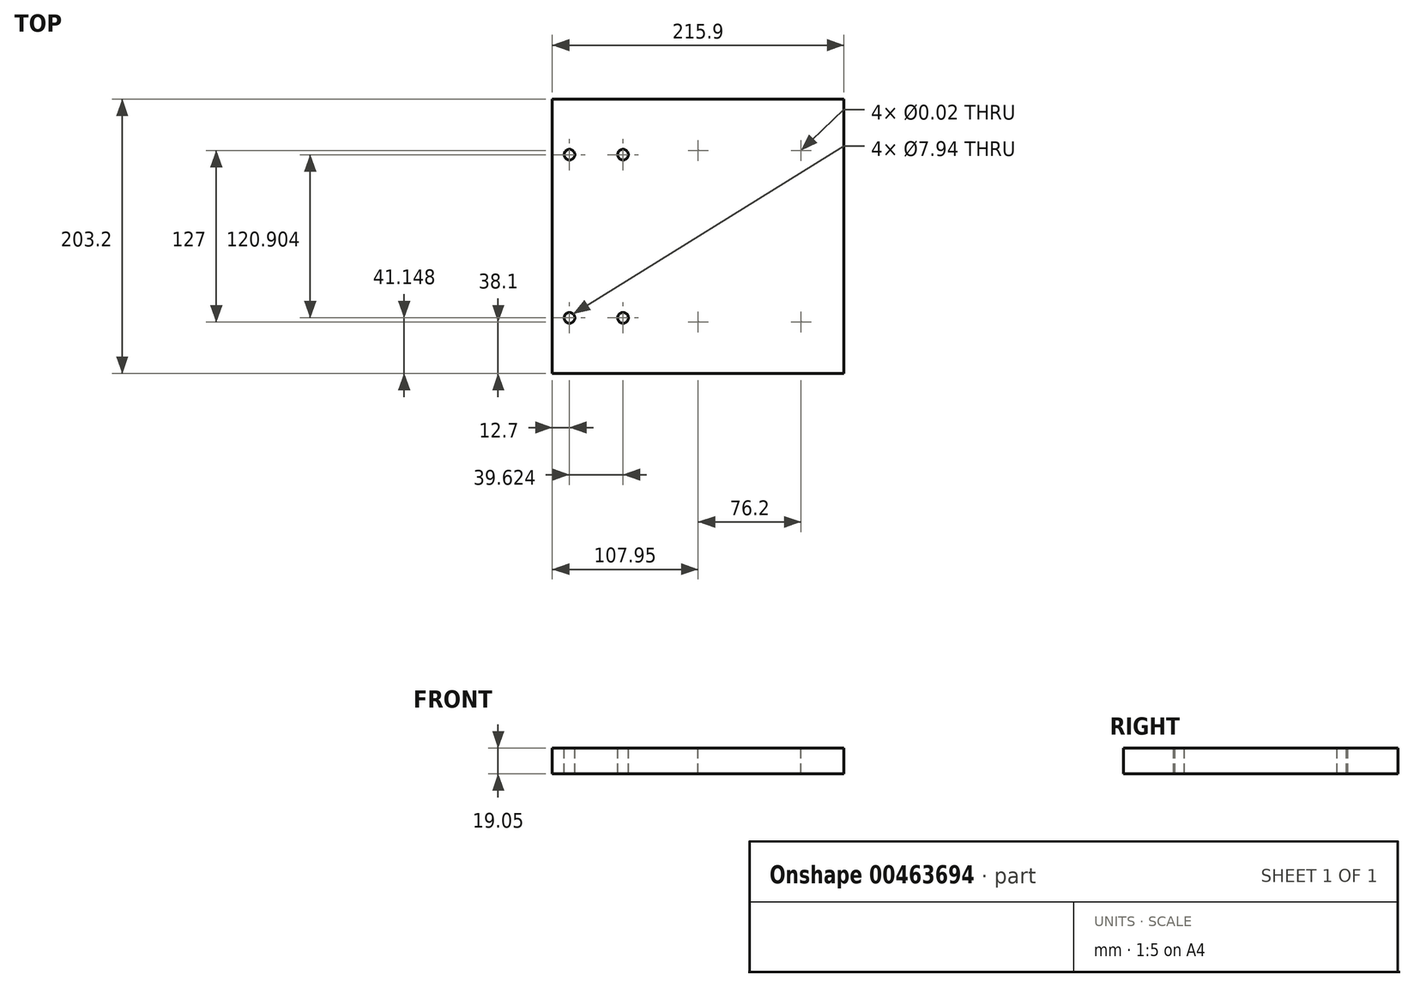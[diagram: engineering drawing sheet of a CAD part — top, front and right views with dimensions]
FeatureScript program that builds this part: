
annotation { "Feature Type Name" : "Feature", "Feature Type Description" : "" }
export const myFeature = defineFeature(function(context is Context, id is Id, definition is map)
    precondition{}
    {
        {
            var Q0;
            Q0=qCreatedBy(makeId("Top.planeOp"),FACE);
            var sketch = newSketch(context, id + "F0", { "sketchPlane" : qUnion([Q0])});
            skLineSegment(sketch, "E0.bottom", {"start": v(-107.95, 101.6) * mm, "end": v(107.95, 101.6) * mm});
            skLineSegment(sketch, "E0.top", {"start": v(-107.95, -101.6) * mm, "end": v(107.95, -101.6) * mm});
            skLineSegment(sketch, "E0.left", {"start": v(-107.95, 101.6) * mm, "end": v(-107.95, -101.6) * mm});
            skLineSegment(sketch, "E0.right", {"start": v(107.95, 101.6) * mm, "end": v(107.95, -101.6) * mm});
            skPoint(sketch, "E0.middle", {"position": v(0, 0) * mm});
            skSolve(sketch);
        }
        {
            var Q0;
            Q0 = qSketchRegion(id + "F0", true);
            extrude(context, id + "F1", {"entities" : qUnion([Q0]), "depth" : 19.05 * mm});
        }
        {
            var Q0;
            Q0=makeQuery(id+"F1.opExtrude","CAP_FACE",FACE,{"disambiguationData":[OSD([sQuery(id+"F0.wireOp",EDGE,"E0.bottom"),sQuery(id+"F0.wireOp",EDGE,"E0.top"),sQuery(id+"F0.wireOp",EDGE,"E0.left"),sQuery(id+"F0.wireOp",EDGE,"E0.right")])],"isStart":false});
            var sketch = newSketch(context, id + "F2", { "sketchPlane" : qUnion([Q0])});
            skLineSegment(sketch, "E1", {"start": v(-145.85, 0) * mm, "end": v(139, 0) * mm, "construction": true});
            skLineSegment(sketch, "E2.0", {"start": v(107.95, 101.6) * mm, "end": v(107.95, -101.6) * mm, "construction": true});
            skLineSegment(sketch, "E3.0", {"start": v(38.1, 101.6) * mm, "end": v(38.1, -101.6) * mm, "construction": true});
            skLineSegment(sketch, "E4.0", {"start": v(0, 101.6) * mm, "end": v(0, -101.6) * mm, "construction": true});
            skLineSegment(sketch, "E5.0", {"start": v(-145.85, -63.5) * mm, "end": v(139, -63.5) * mm, "construction": true});
            skPoint(sketch, "E6", {"position": v(0, -63.5) * mm});
            skPoint(sketch, "E7.MirrorP", {"position": v(0, 63.5) * mm});
            skPoint(sketch, "E8.MirrorP", {"position": v(76.2, 63.5) * mm});
            skPoint(sketch, "E9.MirrorP", {"position": v(76.2, -63.5) * mm});
            skSolve(sketch);
        }
        {
            var Q0;
            Q0=sQuery(id+"F2.wireOp",VERTEX,"E6");
            var Q1;
            Q1=sQuery(id+"F2.wireOp",VERTEX,"E9.MirrorP");
            var Q2;
            Q2=sQuery(id+"F2.wireOp",VERTEX,"E8.MirrorP");
            var Q3;
            Q3=sQuery(id+"F2.wireOp",VERTEX,"E7.MirrorP");
            var Q4;
            Q4=makeQuery(id+"F1.opExtrude","SWEPT_BODY",BODY,{"disambiguationData":[OSD([sQuery(id+"F0.wireOp",EDGE,"E0.bottom"),sQuery(id+"F0.wireOp",EDGE,"E0.top"),sQuery(id+"F0.wireOp",EDGE,"E0.left"),sQuery(id+"F0.wireOp",EDGE,"E0.right")])]});
            hole(context, id + "F3", {"style" : HoleStyle.SIMPLE, "endStyle" : HoleEndStyle.THROUGH, "standardTappedOrClearance" : lookupTablePath({ "standard" : "ANSI", "size" : "7/16 (0.44)", "type" : "Drilled" }), "standardBlindInLast" : lookupTablePath({ "standard" : "ANSI", "size" : "7/16", "type" : "Drilled" }), "holeDiameter" : 7 / 406.4 * mm, "isTappedThrough" : true, "tappedDepth" : 22.22 * mm, "tapClearance" : 3, "locations" : qUnion([Q0, Q1, Q2, Q3]), "scope" : qUnion([Q4])});
        }
        {
            var Q0;
            Q0=makeQuery(id+"F1.opExtrude","CAP_FACE",FACE,{"disambiguationData":[OSD([sQuery(id+"F0.wireOp",EDGE,"E0.bottom"),sQuery(id+"F0.wireOp",EDGE,"E0.top"),sQuery(id+"F0.wireOp",EDGE,"E0.left"),sQuery(id+"F0.wireOp",EDGE,"E0.right")])],"isStart":false});
            var sketch = newSketch(context, id + "F4", { "sketchPlane" : qUnion([Q0])});
            skLineSegment(sketch, "E10.0", {"start": v(-145.85, 0) * mm, "end": v(139, 0) * mm, "construction": true});
            skLineSegment(sketch, "E11.0", {"start": v(-107.95, 101.6) * mm, "end": v(-107.95, -101.6) * mm, "construction": true});
            skLineSegment(sketch, "E12.0", {"start": v(-95.25, 101.6) * mm, "end": v(-95.25, -101.6) * mm, "construction": true});
            skLineSegment(sketch, "E13.0", {"start": v(-55.63, 101.6) * mm, "end": v(-55.63, -101.6) * mm, "construction": true});
            skLineSegment(sketch, "E14.0", {"start": v(-145.85, -60.45) * mm, "end": v(139, -60.45) * mm, "construction": true});
            skPoint(sketch, "E15", {"position": v(-95.25, -60.45) * mm});
            skPoint(sketch, "E16", {"position": v(-55.63, -60.45) * mm});
            skPoint(sketch, "E17.MirrorP", {"position": v(-95.25, 60.45) * mm});
            skPoint(sketch, "E18.MirrorP", {"position": v(-55.63, 60.45) * mm});
            skSolve(sketch);
        }
        {
            var Q0;
            Q0=sQuery(id+"F4.wireOp",VERTEX,"E17.MirrorP");
            var Q1;
            Q1=sQuery(id+"F4.wireOp",VERTEX,"E18.MirrorP");
            var Q2;
            Q2=sQuery(id+"F4.wireOp",VERTEX,"E15");
            var Q3;
            Q3=sQuery(id+"F4.wireOp",VERTEX,"E16");
            var Q4;
            Q4=makeQuery(id+"F1.opExtrude","SWEPT_BODY",BODY,{"disambiguationData":[OSD([sQuery(id+"F0.wireOp",EDGE,"E0.bottom"),sQuery(id+"F0.wireOp",EDGE,"E0.top"),sQuery(id+"F0.wireOp",EDGE,"E0.left"),sQuery(id+"F0.wireOp",EDGE,"E0.right")])]});
            hole(context, id + "F5", {"style" : HoleStyle.SIMPLE, "endStyle" : HoleEndStyle.THROUGH, "standardTappedOrClearance" : lookupTablePath({ "standard" : "ANSI", "engagement" : "75%", "pitch" : "16 tpi", "size" : "3/8", "type" : "Tapped" }), "standardBlindInLast" : lookupTablePath({ "standard" : "ANSI", "engagement" : "75%", "pitch" : "16 tpi", "size" : "3/8", "type" : "Tapped" }), "holeDiameter" : 7.94 * mm, "showTappedDepth" : true, "isTappedThrough" : true, "tappedDepth" : 22.22 * mm, "tapClearance" : 3, "locations" : qUnion([Q0, Q1, Q2, Q3]), "scope" : qUnion([Q4]), "majorDiameter" : 9.53 * mm});
        }
    });
